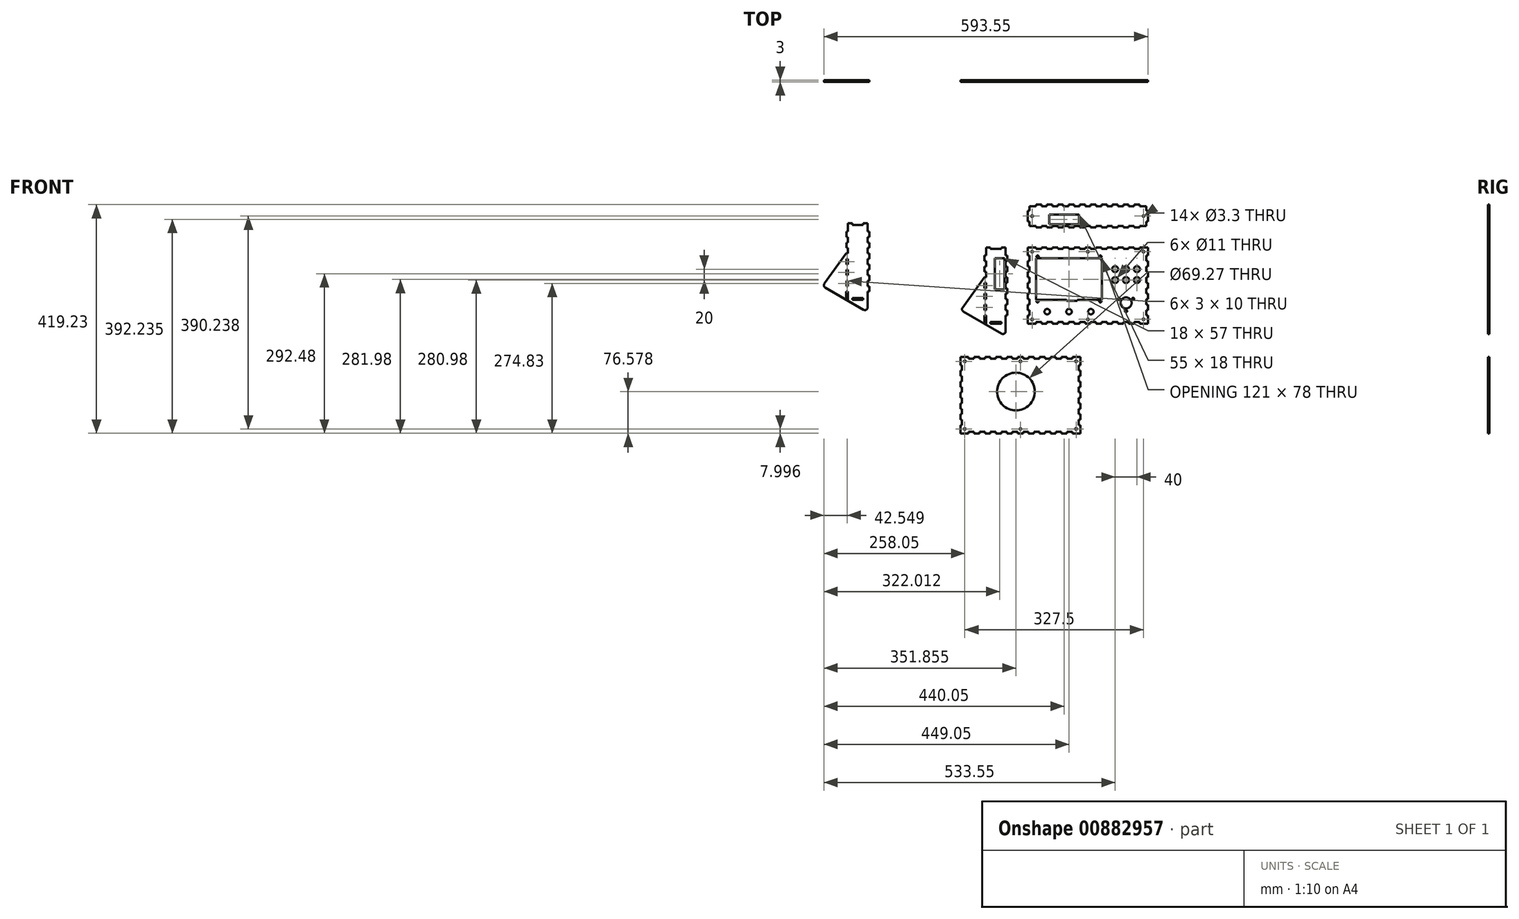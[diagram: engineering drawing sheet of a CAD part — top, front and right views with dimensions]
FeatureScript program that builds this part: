
annotation { "Feature Type Name" : "Feature", "Feature Type Description" : "" }
export const myFeature = defineFeature(function(context is Context, id is Id, definition is map)
    precondition{}
    {
        {
            var Q0;
            Q0=qCreatedBy(makeId("Front.planeOp"),FACE);
            var sketch = newSketch(context, id + "F0", { "sketchPlane" : qUnion([Q0])});
            skLineSegment(sketch, "E0.bottom", {"start": v(-60.5, 38) * mm, "end": v(60.5, 38) * mm});
            skLineSegment(sketch, "E0.top", {"start": v(-60.5, -38) * mm, "end": v(-4.5, -38) * mm});
            skLineSegment(sketch, "E0.left", {"start": v(-60.5, 38) * mm, "end": v(-60.5, -38) * mm});
            skLineSegment(sketch, "E0.right", {"start": v(60.5, 38) * mm, "end": v(60.5, -38) * mm});
            skPoint(sketch, "E0.middle", {"position": v(0, 0) * mm});
            skLineSegment(sketch, "E1.bottom", {"start": v(-75.5, -82) * mm, "end": v(-60.5, -82) * mm});
            skLineSegment(sketch, "E1.top", {"start": v(-75.5, 58) * mm, "end": v(-60.5, 58) * mm});
            skLineSegment(sketch, "E1.left", {"start": v(-75.5, -82) * mm, "end": v(-75.5, -67) * mm});
            skLineSegment(sketch, "E2", {"start": v(-75.5, 43) * mm, "end": v(-72.5, 43) * mm});
            skLineSegment(sketch, "E3", {"start": v(-72.5, 43) * mm, "end": v(-72.5, 33) * mm});
            skLineSegment(sketch, "E4", {"start": v(-72.5, 33) * mm, "end": v(-75.5, 33) * mm});
            skLineSegment(sketch, "E5.0.1.0", {"start": v(-75.5, 23) * mm, "end": v(-72.5, 23) * mm});
            skLineSegment(sketch, "E5.0.1.1", {"start": v(-72.5, 23) * mm, "end": v(-72.5, 13) * mm});
            skLineSegment(sketch, "E5.0.1.2", {"start": v(-72.5, 13) * mm, "end": v(-75.5, 13) * mm});
            skLineSegment(sketch, "E5.0.2.0", {"start": v(-75.5, 3) * mm, "end": v(-72.5, 3) * mm});
            skLineSegment(sketch, "E5.0.2.1", {"start": v(-72.5, 3) * mm, "end": v(-72.5, -7) * mm});
            skLineSegment(sketch, "E5.0.2.2", {"start": v(-72.5, -7) * mm, "end": v(-75.5, -7) * mm});
            skLineSegment(sketch, "E5.0.3.0", {"start": v(-75.5, -17) * mm, "end": v(-72.5, -17) * mm});
            skLineSegment(sketch, "E5.0.3.1", {"start": v(-72.5, -17) * mm, "end": v(-72.5, -27) * mm});
            skLineSegment(sketch, "E5.0.3.2", {"start": v(-72.5, -27) * mm, "end": v(-75.5, -27) * mm});
            skLineSegment(sketch, "E5.0.4.0", {"start": v(-75.5, -37) * mm, "end": v(-72.5, -37) * mm});
            skLineSegment(sketch, "E5.0.4.1", {"start": v(-72.5, -37) * mm, "end": v(-72.5, -47) * mm});
            skLineSegment(sketch, "E5.0.4.2", {"start": v(-72.5, -47) * mm, "end": v(-75.5, -47) * mm});
            skLineSegment(sketch, "E5.0.5.0", {"start": v(-75.5, -57) * mm, "end": v(-72.5, -57) * mm});
            skLineSegment(sketch, "E5.0.5.1", {"start": v(-72.5, -57) * mm, "end": v(-72.5, -67) * mm});
            skLineSegment(sketch, "E5.0.5.2", {"start": v(-72.5, -67) * mm, "end": v(-75.5, -67) * mm});
            skLineSegment(sketch, "E5.direction1", {"start": v(-75.5, 43) * mm, "end": v(-45.5, 43) * mm, "construction": true});
            skLineSegment(sketch, "E5.direction2", {"start": v(-75.5, 33) * mm, "end": v(-75.5, 23) * mm, "construction": true});
            skLineSegment(sketch, "E6.2.0.0", {"start": v(144.5, -79) * mm, "end": v(144.5, -82) * mm});
            skLineSegment(sketch, "E6.4.0.0", {"start": v(99.5, -79) * mm, "end": v(99.5, -82) * mm});
            skLineSegment(sketch, "E6.4.0.1", {"start": v(109.5, -79) * mm, "end": v(99.5, -79) * mm});
            skLineSegment(sketch, "E6.4.0.2", {"start": v(109.5, -82) * mm, "end": v(109.5, -79) * mm});
            skLineSegment(sketch, "E6.5.0.0", {"start": v(79.5, -79) * mm, "end": v(79.5, -82) * mm});
            skLineSegment(sketch, "E6.5.0.1", {"start": v(89.5, -79) * mm, "end": v(79.5, -79) * mm});
            skLineSegment(sketch, "E6.5.0.2", {"start": v(89.5, -82) * mm, "end": v(89.5, -79) * mm});
            skLineSegment(sketch, "E6.6.0.0", {"start": v(59.5, -79) * mm, "end": v(59.5, -82) * mm});
            skLineSegment(sketch, "E6.6.0.1", {"start": v(69.5, -79) * mm, "end": v(59.5, -79) * mm});
            skLineSegment(sketch, "E6.6.0.2", {"start": v(69.5, -82) * mm, "end": v(69.5, -79) * mm});
            skLineSegment(sketch, "E6.7.0.0", {"start": v(39.5, -79) * mm, "end": v(39.5, -82) * mm});
            skLineSegment(sketch, "E6.7.0.1", {"start": v(49.5, -79) * mm, "end": v(39.5, -79) * mm});
            skLineSegment(sketch, "E6.7.0.2", {"start": v(49.5, -82) * mm, "end": v(49.5, -79) * mm});
            skLineSegment(sketch, "E6.8.0.0", {"start": v(19.5, -79) * mm, "end": v(19.5, -82) * mm});
            skLineSegment(sketch, "E6.8.0.1", {"start": v(29.5, -79) * mm, "end": v(19.5, -79) * mm});
            skLineSegment(sketch, "E6.8.0.2", {"start": v(29.5, -82) * mm, "end": v(29.5, -79) * mm});
            skLineSegment(sketch, "E6.9.0.0", {"start": v(-0.5, -79) * mm, "end": v(-0.5, -82) * mm});
            skLineSegment(sketch, "E6.9.0.1", {"start": v(9.5, -79) * mm, "end": v(-0.5, -79) * mm});
            skLineSegment(sketch, "E6.9.0.2", {"start": v(9.5, -82) * mm, "end": v(9.5, -79) * mm});
            skLineSegment(sketch, "E6.10.0.0", {"start": v(-20.5, -79) * mm, "end": v(-20.5, -82) * mm});
            skLineSegment(sketch, "E6.10.0.1", {"start": v(-10.5, -79) * mm, "end": v(-20.5, -79) * mm});
            skLineSegment(sketch, "E6.10.0.2", {"start": v(-10.5, -82) * mm, "end": v(-10.5, -79) * mm});
            skLineSegment(sketch, "E6.11.0.0", {"start": v(-40.5, -79) * mm, "end": v(-40.5, -82) * mm});
            skLineSegment(sketch, "E6.11.0.1", {"start": v(-30.5, -79) * mm, "end": v(-40.5, -79) * mm});
            skLineSegment(sketch, "E6.11.0.2", {"start": v(-30.5, -82) * mm, "end": v(-30.5, -79) * mm});
            skLineSegment(sketch, "E6.12.0.0", {"start": v(-60.5, -79) * mm, "end": v(-60.5, -82) * mm});
            skLineSegment(sketch, "E6.12.0.1", {"start": v(-50.5, -79) * mm, "end": v(-60.5, -79) * mm});
            skLineSegment(sketch, "E6.12.0.2", {"start": v(-50.5, -82) * mm, "end": v(-50.5, -79) * mm});
            skLineSegment(sketch, "E7.2.0.2", {"start": v(144.5, 55) * mm, "end": v(144.5, 58) * mm});
            skLineSegment(sketch, "E7.3.0.0", {"start": v(129.5, 55) * mm, "end": v(119.5, 55) * mm});
            skLineSegment(sketch, "E7.3.0.1", {"start": v(129.5, 58) * mm, "end": v(129.5, 55) * mm});
            skLineSegment(sketch, "E7.3.0.2", {"start": v(119.5, 55) * mm, "end": v(119.5, 58) * mm});
            skLineSegment(sketch, "E7.4.0.0", {"start": v(109.5, 55) * mm, "end": v(99.5, 55) * mm});
            skLineSegment(sketch, "E7.4.0.1", {"start": v(109.5, 58) * mm, "end": v(109.5, 55) * mm});
            skLineSegment(sketch, "E7.4.0.2", {"start": v(99.5, 55) * mm, "end": v(99.5, 58) * mm});
            skLineSegment(sketch, "E7.5.0.0", {"start": v(89.5, 55) * mm, "end": v(79.5, 55) * mm});
            skLineSegment(sketch, "E7.5.0.1", {"start": v(89.5, 58) * mm, "end": v(89.5, 55) * mm});
            skLineSegment(sketch, "E7.5.0.2", {"start": v(79.5, 55) * mm, "end": v(79.5, 58) * mm});
            skLineSegment(sketch, "E7.6.0.0", {"start": v(69.5, 55) * mm, "end": v(59.5, 55) * mm});
            skLineSegment(sketch, "E7.6.0.1", {"start": v(69.5, 58) * mm, "end": v(69.5, 55) * mm});
            skLineSegment(sketch, "E7.6.0.2", {"start": v(59.5, 55) * mm, "end": v(59.5, 58) * mm});
            skLineSegment(sketch, "E7.7.0.0", {"start": v(49.5, 55) * mm, "end": v(39.5, 55) * mm});
            skLineSegment(sketch, "E7.7.0.1", {"start": v(49.5, 58) * mm, "end": v(49.5, 55) * mm});
            skLineSegment(sketch, "E7.7.0.2", {"start": v(39.5, 55) * mm, "end": v(39.5, 58) * mm});
            skLineSegment(sketch, "E7.8.0.0", {"start": v(29.5, 55) * mm, "end": v(19.5, 55) * mm});
            skLineSegment(sketch, "E7.8.0.1", {"start": v(29.5, 58) * mm, "end": v(29.5, 55) * mm});
            skLineSegment(sketch, "E7.8.0.2", {"start": v(19.5, 55) * mm, "end": v(19.5, 58) * mm});
            skLineSegment(sketch, "E7.9.0.0", {"start": v(9.5, 55) * mm, "end": v(-0.5, 55) * mm});
            skLineSegment(sketch, "E7.9.0.1", {"start": v(9.5, 58) * mm, "end": v(9.5, 55) * mm});
            skLineSegment(sketch, "E7.9.0.2", {"start": v(-0.5, 55) * mm, "end": v(-0.5, 58) * mm});
            skLineSegment(sketch, "E7.10.0.0", {"start": v(-10.5, 55) * mm, "end": v(-20.5, 55) * mm});
            skLineSegment(sketch, "E7.10.0.1", {"start": v(-10.5, 58) * mm, "end": v(-10.5, 55) * mm});
            skLineSegment(sketch, "E7.10.0.2", {"start": v(-20.5, 55) * mm, "end": v(-20.5, 58) * mm});
            skLineSegment(sketch, "E7.11.0.0", {"start": v(-30.5, 55) * mm, "end": v(-40.5, 55) * mm});
            skLineSegment(sketch, "E7.11.0.1", {"start": v(-30.5, 58) * mm, "end": v(-30.5, 55) * mm});
            skLineSegment(sketch, "E7.11.0.2", {"start": v(-40.5, 55) * mm, "end": v(-40.5, 58) * mm});
            skLineSegment(sketch, "E7.12.0.0", {"start": v(-50.5, 55) * mm, "end": v(-60.5, 55) * mm});
            skLineSegment(sketch, "E7.12.0.1", {"start": v(-50.5, 58) * mm, "end": v(-50.5, 55) * mm});
            skLineSegment(sketch, "E7.12.0.2", {"start": v(-60.5, 55) * mm, "end": v(-60.5, 58) * mm});
            skLineSegment(sketch, "E8.trimOffspring", {"start": v(-50.5, 58) * mm, "end": v(-40.5, 58) * mm});
            skLineSegment(sketch, "E9.trimOffspring", {"start": v(-30.5, 58) * mm, "end": v(-20.5, 58) * mm});
            skLineSegment(sketch, "E10.trimOffspring", {"start": v(-10.5, 58) * mm, "end": v(-0.5, 58) * mm});
            skLineSegment(sketch, "E11.trimOffspring", {"start": v(9.5, 58) * mm, "end": v(19.5, 58) * mm});
            skLineSegment(sketch, "E12.trimOffspring", {"start": v(29.5, 58) * mm, "end": v(39.5, 58) * mm});
            skLineSegment(sketch, "E13.trimOffspring", {"start": v(49.5, 58) * mm, "end": v(59.5, 58) * mm});
            skLineSegment(sketch, "E14.trimOffspring", {"start": v(69.5, 58) * mm, "end": v(79.5, 58) * mm});
            skLineSegment(sketch, "E15.trimOffspring", {"start": v(89.5, 58) * mm, "end": v(99.5, 58) * mm});
            skLineSegment(sketch, "E16.trimOffspring", {"start": v(109.5, 58) * mm, "end": v(119.5, 58) * mm});
            skLineSegment(sketch, "E17.trimOffspring", {"start": v(-75.5, 23) * mm, "end": v(-75.5, 33) * mm});
            skLineSegment(sketch, "E18.trimOffspring", {"start": v(129.5, 58) * mm, "end": v(144.5, 58) * mm});
            skLineSegment(sketch, "E19.trimOffspring", {"start": v(129.5, -82) * mm, "end": v(144.5, -82) * mm});
            skLineSegment(sketch, "E20.trimOffspring", {"start": v(89.5, -82) * mm, "end": v(99.5, -82) * mm});
            skLineSegment(sketch, "E21.trimOffspring", {"start": v(69.5, -82) * mm, "end": v(79.5, -82) * mm});
            skLineSegment(sketch, "E22.trimOffspring", {"start": v(49.5, -82) * mm, "end": v(59.5, -82) * mm});
            skLineSegment(sketch, "E23.trimOffspring", {"start": v(29.5, -82) * mm, "end": v(39.5, -82) * mm});
            skLineSegment(sketch, "E24.trimOffspring", {"start": v(9.5, -82) * mm, "end": v(19.5, -82) * mm});
            skLineSegment(sketch, "E25.trimOffspring", {"start": v(-10.5, -82) * mm, "end": v(-0.5, -82) * mm});
            skLineSegment(sketch, "E26.trimOffspring", {"start": v(-30.5, -82) * mm, "end": v(-20.5, -82) * mm});
            skLineSegment(sketch, "E27.trimOffspring", {"start": v(-50.5, -82) * mm, "end": v(-40.5, -82) * mm});
            skLineSegment(sketch, "E28.trimOffspring", {"start": v(-75.5, -57) * mm, "end": v(-75.5, -47) * mm});
            skLineSegment(sketch, "E29.trimOffspring", {"start": v(-75.5, -37) * mm, "end": v(-75.5, -27) * mm});
            skLineSegment(sketch, "E30.trimOffspring", {"start": v(-75.5, -17) * mm, "end": v(-75.5, -7) * mm});
            skLineSegment(sketch, "E31.trimOffspring", {"start": v(-75.5, 3) * mm, "end": v(-75.5, 13) * mm});
            skLineSegment(sketch, "E32.trimOffspring", {"start": v(-75.5, 43) * mm, "end": v(-75.5, 58) * mm});
            skLineSegment(sketch, "E33.bottom", {"start": v(-116.04, 58) * mm, "end": v(-124.04, 58) * mm});
            skLineSegment(sketch, "E33.left", {"start": v(-116.04, 58) * mm, "end": v(-116.04, 43) * mm});
            skLineSegment(sketch, "E33.right", {"start": v(-152.04, 58) * mm, "end": v(-152.04, 43) * mm});
            skLineSegment(sketch, "E34", {"start": v(-116.04, 43) * mm, "end": v(-113.04, 43) * mm});
            skLineSegment(sketch, "E35", {"start": v(-113.04, 43) * mm, "end": v(-113.04, 33) * mm});
            skLineSegment(sketch, "E36", {"start": v(-113.04, 33) * mm, "end": v(-116.04, 33) * mm});
            skLineSegment(sketch, "E37.0.1.0", {"start": v(-116.04, 23) * mm, "end": v(-113.04, 23) * mm});
            skLineSegment(sketch, "E37.0.1.1", {"start": v(-113.04, 23) * mm, "end": v(-113.04, 13) * mm});
            skLineSegment(sketch, "E37.0.1.2", {"start": v(-113.04, 13) * mm, "end": v(-116.04, 13) * mm});
            skLineSegment(sketch, "E37.0.2.0", {"start": v(-116.04, 3) * mm, "end": v(-113.04, 3) * mm});
            skLineSegment(sketch, "E37.0.2.1", {"start": v(-113.04, 3) * mm, "end": v(-113.04, -7) * mm});
            skLineSegment(sketch, "E37.0.2.2", {"start": v(-113.04, -7) * mm, "end": v(-116.04, -7) * mm});
            skLineSegment(sketch, "E37.0.3.0", {"start": v(-116.04, -17) * mm, "end": v(-113.04, -17) * mm});
            skLineSegment(sketch, "E37.0.3.1", {"start": v(-113.04, -17) * mm, "end": v(-113.04, -27) * mm});
            skLineSegment(sketch, "E37.0.3.2", {"start": v(-113.04, -27) * mm, "end": v(-116.04, -27) * mm});
            skLineSegment(sketch, "E37.0.4.0", {"start": v(-116.04, -37) * mm, "end": v(-113.04, -37) * mm});
            skLineSegment(sketch, "E37.0.4.1", {"start": v(-113.04, -37) * mm, "end": v(-113.04, -47) * mm});
            skLineSegment(sketch, "E37.0.4.2", {"start": v(-113.04, -47) * mm, "end": v(-116.04, -47) * mm});
            skLineSegment(sketch, "E37.0.5.0", {"start": v(-116.04, -57) * mm, "end": v(-113.04, -57) * mm});
            skLineSegment(sketch, "E37.0.5.1", {"start": v(-113.04, -57) * mm, "end": v(-113.04, -67) * mm});
            skLineSegment(sketch, "E37.0.5.2", {"start": v(-113.04, -67) * mm, "end": v(-116.04, -67) * mm});
            skLineSegment(sketch, "E37.direction1", {"start": v(-116.04, 43) * mm, "end": v(-91.54, 43) * mm, "construction": true});
            skLineSegment(sketch, "E37.direction2", {"start": v(-116.04, 33) * mm, "end": v(-116.04, 23) * mm, "construction": true});
            skLineSegment(sketch, "E38.trimOffspring", {"start": v(-116.04, 13) * mm, "end": v(-116.04, 3) * mm});
            skLineSegment(sketch, "E39.trimOffspring", {"start": v(-116.04, 33) * mm, "end": v(-116.04, 23) * mm});
            skLineSegment(sketch, "E40.trimOffspring", {"start": v(-116.04, -7) * mm, "end": v(-116.04, -17) * mm});
            skLineSegment(sketch, "E41.trimOffspring", {"start": v(-116.04, -27) * mm, "end": v(-116.04, -37) * mm});
            skLineSegment(sketch, "E42.trimOffspring", {"start": v(-116.04, -47) * mm, "end": v(-116.04, -57) * mm});
            skLineSegment(sketch, "E43.trimOffspring", {"start": v(-116.04, -67) * mm, "end": v(-116.04, -82) * mm});
            skLineSegment(sketch, "E44", {"start": v(-152.04, 43) * mm, "end": v(-155.04, 43) * mm});
            skLineSegment(sketch, "E45", {"start": v(-155.04, 43) * mm, "end": v(-155.04, 33) * mm});
            skLineSegment(sketch, "E46", {"start": v(-155.04, 33) * mm, "end": v(-152.04, 33) * mm});
            skLineSegment(sketch, "E47.0.1.0", {"start": v(-152.04, 23) * mm, "end": v(-155.04, 23) * mm});
            skLineSegment(sketch, "E47.0.1.1", {"start": v(-155.04, 23) * mm, "end": v(-155.04, 13) * mm});
            skLineSegment(sketch, "E47.0.1.2", {"start": v(-155.04, 13) * mm, "end": v(-152.04, 13) * mm});
            skLineSegment(sketch, "E47.0.2.0", {"start": v(-152.04, 3) * mm, "end": v(-155.04, 3) * mm});
            skLineSegment(sketch, "E47.0.2.2", {"start": v(-155.04, -7) * mm, "end": v(-152.04, -7) * mm});
            skLineSegment(sketch, "E47.0.3.0", {"start": v(-152.04, -17) * mm, "end": v(-155.04, -17) * mm});
            skLineSegment(sketch, "E47.0.3.2", {"start": v(-155.04, -27) * mm, "end": v(-152.04, -27) * mm});
            skLineSegment(sketch, "E47.0.4.0", {"start": v(-152.04, -37) * mm, "end": v(-155.04, -37) * mm});
            skLineSegment(sketch, "E47.0.4.2", {"start": v(-155.04, -47) * mm, "end": v(-152.04, -47) * mm});
            skLineSegment(sketch, "E47.0.5.0", {"start": v(-152.04, -57) * mm, "end": v(-155.04, -57) * mm});
            skLineSegment(sketch, "E47.0.5.2", {"start": v(-155.04, -67) * mm, "end": v(-152.04, -67) * mm});
            skLineSegment(sketch, "E47.direction1", {"start": v(-155.04, 43) * mm, "end": v(-130.54, 43) * mm, "construction": true});
            skLineSegment(sketch, "E47.direction2", {"start": v(-155.04, 43) * mm, "end": v(-155.04, 23) * mm, "construction": true});
            skLineSegment(sketch, "E48.trimOffspring", {"start": v(-152.04, 33) * mm, "end": v(-152.04, 23) * mm});
            skLineSegment(sketch, "E49.trimOffspring", {"start": v(-152.04, 13) * mm, "end": v(-152.04, 3) * mm});
            skLineSegment(sketch, "E50.trimOffspring", {"start": v(-152.04, -7) * mm, "end": v(-152.04, -17) * mm});
            skLineSegment(sketch, "E51", {"start": v(-155.04, -67) * mm, "end": v(-155.04, -82) * mm});
            skLineSegment(sketch, "E52.trimOffspring", {"start": v(-152.04, -67) * mm, "end": v(-152.04, -82) * mm});
            skLineSegment(sketch, "E53", {"start": v(-155.04, -47) * mm, "end": v(-155.04, -57) * mm});
            skLineSegment(sketch, "E54", {"start": v(-155.04, -27) * mm, "end": v(-155.04, -37) * mm});
            skLineSegment(sketch, "E55.trimOffspring", {"start": v(-152.04, -47) * mm, "end": v(-152.04, -57) * mm});
            skLineSegment(sketch, "E56.trimOffspring", {"start": v(-152.04, -27) * mm, "end": v(-152.04, -37) * mm});
            skLineSegment(sketch, "E57", {"start": v(-155.04, -82) * mm, "end": v(-193.55, -59.77) * mm});
            skLineSegment(sketch, "E58", {"start": v(-155.04, -17) * mm, "end": v(-155.04, -7) * mm});
            skLineSegment(sketch, "E59", {"start": v(-195.1, -52.51) * mm, "end": v(-155.04, 3) * mm});
            skPoint(sketch, "E60.visualSharp", {"position": v(-198.34, -57) * mm});
            skArc(sketch, "E60.filletArc", {"start": v(-195.1, -52.51) * mm, "mid": v(-195.93, -56.48) * mm, "end": v(-193.55, -59.77) * mm});
            skLineSegment(sketch, "E61.bottom", {"start": v(-136.04, 38) * mm, "end": v(-118.04, 38) * mm});
            skLineSegment(sketch, "E61.top", {"start": v(-136.04, -19) * mm, "end": v(-118.04, -19) * mm});
            skLineSegment(sketch, "E61.left", {"start": v(-136.04, 38) * mm, "end": v(-136.04, -19) * mm});
            skLineSegment(sketch, "E61.right", {"start": v(-118.04, 38) * mm, "end": v(-118.04, -19) * mm});
            skLineSegment(sketch, "E62.bottom", {"start": v(-369, 101.85) * mm, "end": v(-377, 101.85) * mm});
            skLineSegment(sketch, "E62.left", {"start": v(-369, 101.85) * mm, "end": v(-369, 86.85) * mm});
            skLineSegment(sketch, "E62.right", {"start": v(-405, 101.85) * mm, "end": v(-405, 86.85) * mm});
            skLineSegment(sketch, "E63", {"start": v(-369, 86.85) * mm, "end": v(-366, 86.85) * mm});
            skLineSegment(sketch, "E64", {"start": v(-366, 86.85) * mm, "end": v(-366, 76.85) * mm});
            skLineSegment(sketch, "E65", {"start": v(-366, 76.85) * mm, "end": v(-369, 76.85) * mm});
            skLineSegment(sketch, "E66.0.1.0", {"start": v(-369, 66.85) * mm, "end": v(-366, 66.85) * mm});
            skLineSegment(sketch, "E66.0.1.1", {"start": v(-366, 66.85) * mm, "end": v(-366, 56.85) * mm});
            skLineSegment(sketch, "E66.0.1.2", {"start": v(-366, 56.85) * mm, "end": v(-369, 56.85) * mm});
            skLineSegment(sketch, "E66.0.2.0", {"start": v(-369, 46.85) * mm, "end": v(-366, 46.85) * mm});
            skLineSegment(sketch, "E66.0.2.1", {"start": v(-366, 46.85) * mm, "end": v(-366, 36.85) * mm});
            skLineSegment(sketch, "E66.0.2.2", {"start": v(-366, 36.85) * mm, "end": v(-369, 36.85) * mm});
            skLineSegment(sketch, "E66.0.3.0", {"start": v(-369, 26.85) * mm, "end": v(-366, 26.85) * mm});
            skLineSegment(sketch, "E66.0.3.1", {"start": v(-366, 26.85) * mm, "end": v(-366, 16.85) * mm});
            skLineSegment(sketch, "E66.0.3.2", {"start": v(-366, 16.85) * mm, "end": v(-369, 16.85) * mm});
            skLineSegment(sketch, "E66.0.4.0", {"start": v(-369, 6.85) * mm, "end": v(-366, 6.85) * mm});
            skLineSegment(sketch, "E66.0.4.1", {"start": v(-366, 6.85) * mm, "end": v(-366, -3.15) * mm});
            skLineSegment(sketch, "E66.0.4.2", {"start": v(-366, -3.15) * mm, "end": v(-369, -3.15) * mm});
            skLineSegment(sketch, "E66.0.5.0", {"start": v(-369, -13.15) * mm, "end": v(-366, -13.15) * mm});
            skLineSegment(sketch, "E66.0.5.1", {"start": v(-366, -13.15) * mm, "end": v(-366, -23.15) * mm});
            skLineSegment(sketch, "E66.0.5.2", {"start": v(-366, -23.15) * mm, "end": v(-369, -23.15) * mm});
            skLineSegment(sketch, "E66.direction2", {"start": v(-369, 76.85) * mm, "end": v(-369, 66.85) * mm, "construction": true});
            skLineSegment(sketch, "E67.trimOffspring", {"start": v(-369, 56.85) * mm, "end": v(-369, 46.85) * mm});
            skLineSegment(sketch, "E68.trimOffspring", {"start": v(-369, 76.85) * mm, "end": v(-369, 66.85) * mm});
            skLineSegment(sketch, "E69.trimOffspring", {"start": v(-369, 36.85) * mm, "end": v(-369, 26.85) * mm});
            skLineSegment(sketch, "E70.trimOffspring", {"start": v(-369, 16.85) * mm, "end": v(-369, 6.85) * mm});
            skLineSegment(sketch, "E71.trimOffspring", {"start": v(-369, -3.15) * mm, "end": v(-369, -13.15) * mm});
            skLineSegment(sketch, "E72.trimOffspring", {"start": v(-369, -23.15) * mm, "end": v(-369, -38.15) * mm});
            skLineSegment(sketch, "E73", {"start": v(-405, 86.85) * mm, "end": v(-408, 86.85) * mm});
            skLineSegment(sketch, "E74", {"start": v(-408, 86.85) * mm, "end": v(-408, 76.85) * mm});
            skLineSegment(sketch, "E75", {"start": v(-408, 76.85) * mm, "end": v(-405, 76.85) * mm});
            skLineSegment(sketch, "E76.0.1.0", {"start": v(-405, 66.85) * mm, "end": v(-408, 66.85) * mm});
            skLineSegment(sketch, "E76.0.1.1", {"start": v(-408, 66.85) * mm, "end": v(-408, 56.85) * mm});
            skLineSegment(sketch, "E76.0.1.2", {"start": v(-408, 56.85) * mm, "end": v(-405, 56.85) * mm});
            skLineSegment(sketch, "E76.0.2.0", {"start": v(-405, 46.85) * mm, "end": v(-408.04, 46.85) * mm});
            skLineSegment(sketch, "E76.0.2.2", {"start": v(-408, 36.85) * mm, "end": v(-405, 36.85) * mm});
            skLineSegment(sketch, "E76.0.3.0", {"start": v(-405, 26.85) * mm, "end": v(-408, 26.85) * mm});
            skLineSegment(sketch, "E76.0.3.2", {"start": v(-408, 16.85) * mm, "end": v(-405, 16.85) * mm});
            skLineSegment(sketch, "E76.0.4.0", {"start": v(-405, 6.85) * mm, "end": v(-408, 6.85) * mm});
            skLineSegment(sketch, "E76.0.4.2", {"start": v(-408, -3.15) * mm, "end": v(-405, -3.15) * mm});
            skLineSegment(sketch, "E76.0.5.0", {"start": v(-405, -13.15) * mm, "end": v(-408, -13.15) * mm});
            skLineSegment(sketch, "E76.0.5.2", {"start": v(-408.04, -23.15) * mm, "end": v(-405, -23.15) * mm});
            skLineSegment(sketch, "E76.direction1", {"start": v(-408, 86.85) * mm, "end": v(-383.04, 86.85) * mm, "construction": true});
            skLineSegment(sketch, "E76.direction2", {"start": v(-408, 86.85) * mm, "end": v(-408, 66.85) * mm, "construction": true});
            skLineSegment(sketch, "E77.trimOffspring", {"start": v(-405, 76.85) * mm, "end": v(-405, 66.85) * mm});
            skLineSegment(sketch, "E78.trimOffspring", {"start": v(-405, 56.85) * mm, "end": v(-405, 46.85) * mm});
            skLineSegment(sketch, "E79.trimOffspring", {"start": v(-405, 36.85) * mm, "end": v(-405, 26.85) * mm});
            skLineSegment(sketch, "E80", {"start": v(-408.04, -23.15) * mm, "end": v(-408.04, -38.14) * mm});
            skLineSegment(sketch, "E81.trimOffspring", {"start": v(-405, -23.15) * mm, "end": v(-405, -38.15) * mm});
            skLineSegment(sketch, "E82", {"start": v(-408, -3.15) * mm, "end": v(-408, -13.15) * mm});
            skLineSegment(sketch, "E83", {"start": v(-408, 16.85) * mm, "end": v(-408, 6.85) * mm});
            skLineSegment(sketch, "E84.trimOffspring", {"start": v(-405, -3.15) * mm, "end": v(-405, -13.15) * mm});
            skLineSegment(sketch, "E85.trimOffspring", {"start": v(-405, 16.85) * mm, "end": v(-405, 6.85) * mm});
            skLineSegment(sketch, "E86", {"start": v(-408.04, -38.15) * mm, "end": v(-446.55, -15.92) * mm});
            skLineSegment(sketch, "E87", {"start": v(-408, 26.85) * mm, "end": v(-408, 36.85) * mm});
            skLineSegment(sketch, "E88", {"start": v(-448.1, -8.66) * mm, "end": v(-408.04, 46.85) * mm});
            skPoint(sketch, "E89.visualSharp", {"position": v(-451.35, -13.15) * mm});
            skArc(sketch, "E89.filletArc", {"start": v(-448.1, -8.66) * mm, "mid": v(-448.94, -12.63) * mm, "end": v(-446.55, -15.92) * mm});
            skLineSegment(sketch, "E90.top", {"start": v(-199, -142.98) * mm, "end": v(-184, -142.98) * mm});
            skLineSegment(sketch, "E90.left", {"start": v(-199, -282.98) * mm, "end": v(-199, -267.98) * mm});
            skLineSegment(sketch, "E91", {"start": v(-199, -157.98) * mm, "end": v(-196, -157.98) * mm});
            skLineSegment(sketch, "E92", {"start": v(-196, -157.98) * mm, "end": v(-196, -167.98) * mm});
            skLineSegment(sketch, "E93", {"start": v(-196, -167.98) * mm, "end": v(-199, -167.98) * mm});
            skLineSegment(sketch, "E94.0.1.0", {"start": v(-199, -177.98) * mm, "end": v(-196, -177.98) * mm});
            skLineSegment(sketch, "E94.0.1.1", {"start": v(-196, -177.98) * mm, "end": v(-196, -187.98) * mm});
            skLineSegment(sketch, "E94.0.1.2", {"start": v(-196, -187.98) * mm, "end": v(-199, -187.98) * mm});
            skLineSegment(sketch, "E94.0.2.0", {"start": v(-199, -197.98) * mm, "end": v(-196, -197.98) * mm});
            skLineSegment(sketch, "E94.0.2.1", {"start": v(-196, -197.98) * mm, "end": v(-196, -207.98) * mm});
            skLineSegment(sketch, "E94.0.2.2", {"start": v(-196, -207.98) * mm, "end": v(-199, -207.98) * mm});
            skLineSegment(sketch, "E94.0.3.0", {"start": v(-199, -217.98) * mm, "end": v(-196, -217.98) * mm});
            skLineSegment(sketch, "E94.0.3.1", {"start": v(-196, -217.98) * mm, "end": v(-196, -227.98) * mm});
            skLineSegment(sketch, "E94.0.3.2", {"start": v(-196, -227.98) * mm, "end": v(-199, -227.98) * mm});
            skLineSegment(sketch, "E94.0.4.0", {"start": v(-199, -237.98) * mm, "end": v(-196, -237.98) * mm});
            skLineSegment(sketch, "E94.0.4.1", {"start": v(-196, -237.98) * mm, "end": v(-196, -247.98) * mm});
            skLineSegment(sketch, "E94.0.4.2", {"start": v(-196, -247.98) * mm, "end": v(-199, -247.98) * mm});
            skLineSegment(sketch, "E94.0.5.0", {"start": v(-199, -257.98) * mm, "end": v(-196, -257.98) * mm});
            skLineSegment(sketch, "E94.0.5.1", {"start": v(-196, -257.98) * mm, "end": v(-196, -267.98) * mm});
            skLineSegment(sketch, "E94.0.5.2", {"start": v(-196, -267.98) * mm, "end": v(-199, -267.98) * mm});
            skLineSegment(sketch, "E94.direction2", {"start": v(-199, -167.98) * mm, "end": v(-199, -177.98) * mm, "construction": true});
            skLineSegment(sketch, "E95.2.0.2", {"start": v(21, -145.98) * mm, "end": v(21, -142.98) * mm});
            skLineSegment(sketch, "E95.3.0.0", {"start": v(6, -145.98) * mm, "end": v(-4, -145.98) * mm});
            skLineSegment(sketch, "E95.3.0.1", {"start": v(6, -142.98) * mm, "end": v(6, -145.98) * mm});
            skLineSegment(sketch, "E95.3.0.2", {"start": v(-4, -145.98) * mm, "end": v(-4, -142.98) * mm});
            skLineSegment(sketch, "E95.4.0.0", {"start": v(-14, -145.98) * mm, "end": v(-24, -145.98) * mm});
            skLineSegment(sketch, "E95.4.0.1", {"start": v(-14, -142.98) * mm, "end": v(-14, -145.98) * mm});
            skLineSegment(sketch, "E95.4.0.2", {"start": v(-24, -145.98) * mm, "end": v(-24, -142.98) * mm});
            skLineSegment(sketch, "E95.5.0.0", {"start": v(-34, -145.98) * mm, "end": v(-44, -145.98) * mm});
            skLineSegment(sketch, "E95.5.0.1", {"start": v(-34, -142.98) * mm, "end": v(-34, -145.98) * mm});
            skLineSegment(sketch, "E95.5.0.2", {"start": v(-44, -145.98) * mm, "end": v(-44, -142.98) * mm});
            skLineSegment(sketch, "E95.6.0.0", {"start": v(-54, -145.98) * mm, "end": v(-64, -145.98) * mm});
            skLineSegment(sketch, "E95.6.0.1", {"start": v(-54, -142.98) * mm, "end": v(-54, -145.98) * mm});
            skLineSegment(sketch, "E95.6.0.2", {"start": v(-64, -145.98) * mm, "end": v(-64, -142.98) * mm});
            skLineSegment(sketch, "E95.7.0.0", {"start": v(-74, -145.98) * mm, "end": v(-84, -145.98) * mm});
            skLineSegment(sketch, "E95.7.0.1", {"start": v(-74, -142.98) * mm, "end": v(-74, -145.98) * mm});
            skLineSegment(sketch, "E95.7.0.2", {"start": v(-84, -145.98) * mm, "end": v(-84, -142.98) * mm});
            skLineSegment(sketch, "E95.8.0.0", {"start": v(-94, -145.98) * mm, "end": v(-104, -145.98) * mm});
            skLineSegment(sketch, "E95.8.0.1", {"start": v(-94, -142.98) * mm, "end": v(-94, -145.98) * mm});
            skLineSegment(sketch, "E95.8.0.2", {"start": v(-104, -145.98) * mm, "end": v(-104, -142.98) * mm});
            skLineSegment(sketch, "E95.9.0.0", {"start": v(-114, -145.98) * mm, "end": v(-124, -145.98) * mm});
            skLineSegment(sketch, "E95.9.0.1", {"start": v(-114, -142.98) * mm, "end": v(-114, -145.98) * mm});
            skLineSegment(sketch, "E95.9.0.2", {"start": v(-124, -145.98) * mm, "end": v(-124, -142.98) * mm});
            skLineSegment(sketch, "E95.10.0.0", {"start": v(-134, -145.98) * mm, "end": v(-144, -145.98) * mm});
            skLineSegment(sketch, "E95.10.0.1", {"start": v(-134, -142.98) * mm, "end": v(-134, -145.98) * mm});
            skLineSegment(sketch, "E95.10.0.2", {"start": v(-144, -145.98) * mm, "end": v(-144, -142.98) * mm});
            skLineSegment(sketch, "E95.11.0.0", {"start": v(-154, -145.98) * mm, "end": v(-164, -145.98) * mm});
            skLineSegment(sketch, "E95.11.0.1", {"start": v(-154, -142.98) * mm, "end": v(-154, -145.98) * mm});
            skLineSegment(sketch, "E95.11.0.2", {"start": v(-164, -145.98) * mm, "end": v(-164, -142.98) * mm});
            skLineSegment(sketch, "E95.12.0.0", {"start": v(-174, -145.98) * mm, "end": v(-184, -145.98) * mm});
            skLineSegment(sketch, "E95.12.0.1", {"start": v(-174, -142.98) * mm, "end": v(-174, -145.98) * mm});
            skLineSegment(sketch, "E95.12.0.2", {"start": v(-184, -145.98) * mm, "end": v(-184, -142.98) * mm});
            skLineSegment(sketch, "E96.trimOffspring", {"start": v(-174, -142.98) * mm, "end": v(-164, -142.98) * mm});
            skLineSegment(sketch, "E97.trimOffspring", {"start": v(-154, -142.98) * mm, "end": v(-144, -142.98) * mm});
            skLineSegment(sketch, "E98.trimOffspring", {"start": v(-134, -142.98) * mm, "end": v(-124, -142.98) * mm});
            skLineSegment(sketch, "E99.trimOffspring", {"start": v(-114, -142.98) * mm, "end": v(-104, -142.98) * mm});
            skLineSegment(sketch, "E100.trimOffspring", {"start": v(-94, -142.98) * mm, "end": v(-84, -142.98) * mm});
            skLineSegment(sketch, "E101.trimOffspring", {"start": v(-74, -142.98) * mm, "end": v(-64, -142.98) * mm});
            skLineSegment(sketch, "E102.trimOffspring", {"start": v(-54, -142.98) * mm, "end": v(-44, -142.98) * mm});
            skLineSegment(sketch, "E103.trimOffspring", {"start": v(-34, -142.98) * mm, "end": v(-24, -142.98) * mm});
            skLineSegment(sketch, "E104.trimOffspring", {"start": v(-14, -142.98) * mm, "end": v(-4, -142.98) * mm});
            skLineSegment(sketch, "E105.trimOffspring", {"start": v(-199, -177.98) * mm, "end": v(-199, -167.98) * mm});
            skLineSegment(sketch, "E106.trimOffspring", {"start": v(6, -142.98) * mm, "end": v(21, -142.98) * mm});
            skLineSegment(sketch, "E107.trimOffspring", {"start": v(-199, -257.98) * mm, "end": v(-199, -247.98) * mm});
            skLineSegment(sketch, "E108.trimOffspring", {"start": v(-199, -237.98) * mm, "end": v(-199, -227.98) * mm});
            skLineSegment(sketch, "E109.trimOffspring", {"start": v(-199, -217.98) * mm, "end": v(-199, -207.98) * mm});
            skLineSegment(sketch, "E110.trimOffspring", {"start": v(-199, -197.98) * mm, "end": v(-199, -187.98) * mm});
            skLineSegment(sketch, "E111.trimOffspring", {"start": v(-199, -157.98) * mm, "end": v(-199, -142.98) * mm});
            skLineSegment(sketch, "E112.bottom", {"start": v(-60.5, 94.25) * mm, "end": v(-50.5, 94.25) * mm});
            skLineSegment(sketch, "E112.top", {"start": v(-60.5, 136.25) * mm, "end": v(-50.5, 136.25) * mm});
            skLineSegment(sketch, "E112.left", {"start": v(-75.5, 105.25) * mm, "end": v(-75.5, 125.25) * mm});
            skLineSegment(sketch, "E113", {"start": v(-60.5, 94.25) * mm, "end": v(-60.5, 97.25) * mm});
            skLineSegment(sketch, "E114", {"start": v(-60.5, 97.25) * mm, "end": v(-72.5, 97.25) * mm});
            skPoint(sketch, "E115.orphan", {"position": v(-75.5, 94.25) * mm});
            skLineSegment(sketch, "E116", {"start": v(-50.5, 94.25) * mm, "end": v(-50.5, 97.25) * mm});
            skLineSegment(sketch, "E117", {"start": v(-50.5, 97.25) * mm, "end": v(-40.5, 97.25) * mm});
            skLineSegment(sketch, "E118", {"start": v(-40.5, 97.25) * mm, "end": v(-40.5, 94.25) * mm});
            skLineSegment(sketch, "E119.trimOffspring", {"start": v(-40.5, 94.25) * mm, "end": v(-30.5, 94.25) * mm});
            skLineSegment(sketch, "E120.1.0.0", {"start": v(-30.5, 94.25) * mm, "end": v(-30.5, 97.25) * mm});
            skLineSegment(sketch, "E120.1.0.1", {"start": v(-30.5, 97.25) * mm, "end": v(-20.5, 97.25) * mm});
            skLineSegment(sketch, "E120.1.0.2", {"start": v(-20.5, 97.25) * mm, "end": v(-20.5, 94.25) * mm});
            skLineSegment(sketch, "E120.2.0.0", {"start": v(-10.5, 94.25) * mm, "end": v(-10.5, 97.25) * mm});
            skLineSegment(sketch, "E120.2.0.1", {"start": v(-10.5, 97.25) * mm, "end": v(-0.5, 97.25) * mm});
            skLineSegment(sketch, "E120.2.0.2", {"start": v(-0.5, 97.25) * mm, "end": v(-0.5, 94.25) * mm});
            skLineSegment(sketch, "E120.3.0.0", {"start": v(9.5, 94.25) * mm, "end": v(9.5, 97.25) * mm});
            skLineSegment(sketch, "E120.3.0.1", {"start": v(9.5, 97.25) * mm, "end": v(19.5, 97.25) * mm});
            skLineSegment(sketch, "E120.3.0.2", {"start": v(19.5, 97.25) * mm, "end": v(19.5, 94.25) * mm});
            skLineSegment(sketch, "E120.4.0.0", {"start": v(29.5, 94.25) * mm, "end": v(29.5, 97.25) * mm});
            skLineSegment(sketch, "E120.4.0.1", {"start": v(29.5, 97.25) * mm, "end": v(39.5, 97.25) * mm});
            skLineSegment(sketch, "E120.4.0.2", {"start": v(39.5, 97.25) * mm, "end": v(39.5, 94.25) * mm});
            skLineSegment(sketch, "E120.5.0.0", {"start": v(49.5, 94.25) * mm, "end": v(49.5, 97.25) * mm});
            skLineSegment(sketch, "E120.5.0.1", {"start": v(49.5, 97.25) * mm, "end": v(59.5, 97.25) * mm});
            skLineSegment(sketch, "E120.5.0.2", {"start": v(59.5, 97.25) * mm, "end": v(59.5, 94.25) * mm});
            skLineSegment(sketch, "E120.6.0.0", {"start": v(69.5, 94.25) * mm, "end": v(69.5, 97.25) * mm});
            skLineSegment(sketch, "E120.6.0.1", {"start": v(69.5, 97.25) * mm, "end": v(79.5, 97.25) * mm});
            skLineSegment(sketch, "E120.6.0.2", {"start": v(79.5, 97.25) * mm, "end": v(79.5, 94.25) * mm});
            skLineSegment(sketch, "E120.7.0.0", {"start": v(89.5, 94.25) * mm, "end": v(89.5, 97.25) * mm});
            skLineSegment(sketch, "E120.7.0.1", {"start": v(89.5, 97.25) * mm, "end": v(99.5, 97.25) * mm});
            skLineSegment(sketch, "E120.7.0.2", {"start": v(99.5, 97.25) * mm, "end": v(99.5, 94.25) * mm});
            skLineSegment(sketch, "E120.8.0.0", {"start": v(109.5, 94.25) * mm, "end": v(109.5, 97.25) * mm});
            skLineSegment(sketch, "E120.8.0.1", {"start": v(109.5, 97.25) * mm, "end": v(119.5, 97.25) * mm});
            skLineSegment(sketch, "E120.8.0.2", {"start": v(119.5, 97.25) * mm, "end": v(119.5, 94.25) * mm});
            skLineSegment(sketch, "E120.9.0.0", {"start": v(129.5, 94.25) * mm, "end": v(129.5, 97.25) * mm});
            skLineSegment(sketch, "E120.9.0.1", {"start": v(129.5, 97.25) * mm, "end": v(139.5, 97.25) * mm});
            skLineSegment(sketch, "E120.direction1", {"start": v(-40.5, 94.25) * mm, "end": v(-30.5, 94.25) * mm, "construction": true});
            skLineSegment(sketch, "E121.trimOffspring", {"start": v(-20.5, 94.25) * mm, "end": v(-10.5, 94.25) * mm});
            skLineSegment(sketch, "E122.trimOffspring", {"start": v(-0.5, 94.25) * mm, "end": v(9.5, 94.25) * mm});
            skLineSegment(sketch, "E123.trimOffspring", {"start": v(19.5, 94.25) * mm, "end": v(29.5, 94.25) * mm});
            skLineSegment(sketch, "E124.trimOffspring", {"start": v(39.5, 94.25) * mm, "end": v(49.5, 94.25) * mm});
            skLineSegment(sketch, "E125.trimOffspring", {"start": v(59.5, 94.25) * mm, "end": v(69.5, 94.25) * mm});
            skLineSegment(sketch, "E126.trimOffspring", {"start": v(79.5, 94.25) * mm, "end": v(89.5, 94.25) * mm});
            skLineSegment(sketch, "E127.trimOffspring", {"start": v(99.5, 94.25) * mm, "end": v(109.5, 94.25) * mm});
            skLineSegment(sketch, "E128.trimOffspring", {"start": v(119.5, 94.25) * mm, "end": v(129.5, 94.25) * mm});
            skLineSegment(sketch, "E129", {"start": v(-60.5, 136.25) * mm, "end": v(-60.5, 133.25) * mm});
            skLineSegment(sketch, "E130", {"start": v(-60.5, 133.25) * mm, "end": v(-72.5, 133.25) * mm});
            skLineSegment(sketch, "E131", {"start": v(-50.5, 136.25) * mm, "end": v(-50.5, 133.25) * mm});
            skLineSegment(sketch, "E132", {"start": v(-50.5, 133.25) * mm, "end": v(-40.5, 133.25) * mm});
            skLineSegment(sketch, "E133", {"start": v(-40.5, 133.25) * mm, "end": v(-40.5, 136.25) * mm});
            skLineSegment(sketch, "E134.trimOffspring", {"start": v(-40.5, 136.25) * mm, "end": v(-30.5, 136.25) * mm});
            skLineSegment(sketch, "E135.1.0.0", {"start": v(-30.5, 136.25) * mm, "end": v(-30.5, 133.25) * mm});
            skLineSegment(sketch, "E135.1.0.1", {"start": v(-30.5, 133.25) * mm, "end": v(-20.5, 133.25) * mm});
            skLineSegment(sketch, "E135.1.0.2", {"start": v(-20.5, 133.25) * mm, "end": v(-20.5, 136.25) * mm});
            skLineSegment(sketch, "E135.2.0.0", {"start": v(-10.5, 136.25) * mm, "end": v(-10.5, 133.25) * mm});
            skLineSegment(sketch, "E135.2.0.1", {"start": v(-10.5, 133.25) * mm, "end": v(-0.5, 133.25) * mm});
            skLineSegment(sketch, "E135.2.0.2", {"start": v(-0.5, 133.25) * mm, "end": v(-0.5, 136.25) * mm});
            skLineSegment(sketch, "E135.3.0.0", {"start": v(9.5, 136.25) * mm, "end": v(9.5, 133.25) * mm});
            skLineSegment(sketch, "E135.3.0.1", {"start": v(9.5, 133.25) * mm, "end": v(19.5, 133.25) * mm});
            skLineSegment(sketch, "E135.3.0.2", {"start": v(19.5, 133.25) * mm, "end": v(19.5, 136.25) * mm});
            skLineSegment(sketch, "E135.4.0.0", {"start": v(29.5, 136.25) * mm, "end": v(29.5, 133.25) * mm});
            skLineSegment(sketch, "E135.4.0.1", {"start": v(29.5, 133.25) * mm, "end": v(39.5, 133.25) * mm});
            skLineSegment(sketch, "E135.4.0.2", {"start": v(39.5, 133.25) * mm, "end": v(39.5, 136.25) * mm});
            skLineSegment(sketch, "E135.5.0.0", {"start": v(49.5, 136.25) * mm, "end": v(49.5, 133.25) * mm});
            skLineSegment(sketch, "E135.5.0.1", {"start": v(49.5, 133.25) * mm, "end": v(59.5, 133.25) * mm});
            skLineSegment(sketch, "E135.5.0.2", {"start": v(59.5, 133.25) * mm, "end": v(59.5, 136.25) * mm});
            skLineSegment(sketch, "E135.6.0.0", {"start": v(69.5, 136.25) * mm, "end": v(69.5, 133.25) * mm});
            skLineSegment(sketch, "E135.6.0.1", {"start": v(69.5, 133.25) * mm, "end": v(79.5, 133.25) * mm});
            skLineSegment(sketch, "E135.6.0.2", {"start": v(79.5, 133.25) * mm, "end": v(79.5, 136.25) * mm});
            skLineSegment(sketch, "E135.7.0.0", {"start": v(89.5, 136.25) * mm, "end": v(89.5, 133.25) * mm});
            skLineSegment(sketch, "E135.7.0.1", {"start": v(89.5, 133.25) * mm, "end": v(99.5, 133.25) * mm});
            skLineSegment(sketch, "E135.7.0.2", {"start": v(99.5, 133.25) * mm, "end": v(99.5, 136.25) * mm});
            skLineSegment(sketch, "E135.8.0.0", {"start": v(109.5, 136.25) * mm, "end": v(109.5, 133.25) * mm});
            skLineSegment(sketch, "E135.8.0.1", {"start": v(109.5, 133.25) * mm, "end": v(119.5, 133.25) * mm});
            skLineSegment(sketch, "E135.8.0.2", {"start": v(119.5, 133.25) * mm, "end": v(119.5, 136.25) * mm});
            skLineSegment(sketch, "E135.9.0.0", {"start": v(129.5, 136.25) * mm, "end": v(129.5, 133.25) * mm});
            skLineSegment(sketch, "E135.9.0.1", {"start": v(129.5, 133.25) * mm, "end": v(139.5, 133.25) * mm});
            skLineSegment(sketch, "E135.direction1", {"start": v(-50.5, 133.25) * mm, "end": v(-30.5, 133.25) * mm, "construction": true});
            skLineSegment(sketch, "E136.trimOffspring", {"start": v(-20.5, 136.25) * mm, "end": v(-10.5, 136.25) * mm});
            skLineSegment(sketch, "E137.trimOffspring", {"start": v(-0.5, 136.25) * mm, "end": v(9.5, 136.25) * mm});
            skLineSegment(sketch, "E138.trimOffspring", {"start": v(19.5, 136.25) * mm, "end": v(29.5, 136.25) * mm});
            skLineSegment(sketch, "E139.trimOffspring", {"start": v(39.5, 136.25) * mm, "end": v(49.5, 136.25) * mm});
            skLineSegment(sketch, "E140.trimOffspring", {"start": v(59.5, 136.25) * mm, "end": v(69.5, 136.25) * mm});
            skLineSegment(sketch, "E141.trimOffspring", {"start": v(79.5, 136.25) * mm, "end": v(89.5, 136.25) * mm});
            skLineSegment(sketch, "E142.trimOffspring", {"start": v(99.5, 136.25) * mm, "end": v(109.5, 136.25) * mm});
            skLineSegment(sketch, "E143.trimOffspring", {"start": v(119.5, 136.25) * mm, "end": v(129.5, 136.25) * mm});
            skLineSegment(sketch, "E144", {"start": v(-144.04, 58) * mm, "end": v(-144.04, 55) * mm});
            skLineSegment(sketch, "E145", {"start": v(-144.04, 55) * mm, "end": v(-124.04, 55) * mm});
            skLineSegment(sketch, "E146", {"start": v(-124.04, 55) * mm, "end": v(-124.04, 58) * mm});
            skLineSegment(sketch, "E147.trimOffspring", {"start": v(-144.04, 58) * mm, "end": v(-152.04, 58) * mm});
            skLineSegment(sketch, "E148", {"start": v(-144.04, -82) * mm, "end": v(-144.04, -79) * mm});
            skLineSegment(sketch, "E149", {"start": v(-144.04, -79) * mm, "end": v(-124.04, -79) * mm});
            skLineSegment(sketch, "E150", {"start": v(-124.04, -79) * mm, "end": v(-124.04, -82) * mm});
            skLineSegment(sketch, "E151", {"start": v(-72.5, 133.25) * mm, "end": v(-72.5, 125.25) * mm});
            skLineSegment(sketch, "E152", {"start": v(-72.5, 125.25) * mm, "end": v(-75.5, 125.25) * mm});
            skLineSegment(sketch, "E153", {"start": v(-72.5, 97.25) * mm, "end": v(-72.5, 105.25) * mm});
            skLineSegment(sketch, "E154", {"start": v(-72.5, 105.25) * mm, "end": v(-75.5, 105.25) * mm});
            skPoint(sketch, "E155.orphan", {"position": v(-75.5, 97.25) * mm});
            skLineSegment(sketch, "E156.bottom", {"start": v(-36.5, 118.25) * mm, "end": v(18.5, 118.25) * mm});
            skLineSegment(sketch, "E156.top", {"start": v(-36.5, 100.25) * mm, "end": v(18.5, 100.25) * mm});
            skLineSegment(sketch, "E156.left", {"start": v(-36.5, 118.25) * mm, "end": v(-36.5, 100.25) * mm});
            skLineSegment(sketch, "E156.right", {"start": v(18.5, 118.25) * mm, "end": v(18.5, 100.25) * mm});
            skLineSegment(sketch, "E157.2.0.3", {"start": v(21, -282.98) * mm, "end": v(11, -282.98) * mm});
            skLineSegment(sketch, "E157.3.0.0", {"start": v(6, -282.98) * mm, "end": v(6, -279.98) * mm});
            skLineSegment(sketch, "E157.3.0.1", {"start": v(6, -279.98) * mm, "end": v(-4, -279.98) * mm});
            skLineSegment(sketch, "E157.3.0.2", {"start": v(-4, -279.98) * mm, "end": v(-4, -282.98) * mm});
            skLineSegment(sketch, "E157.3.0.3", {"start": v(-4, -282.98) * mm, "end": v(-14, -282.98) * mm});
            skLineSegment(sketch, "E157.12.0.0", {"start": v(-174, -282.98) * mm, "end": v(-174, -279.98) * mm});
            skLineSegment(sketch, "E157.12.0.1", {"start": v(-174, -279.98) * mm, "end": v(-184, -279.98) * mm});
            skLineSegment(sketch, "E157.12.0.2", {"start": v(-184, -279.98) * mm, "end": v(-184, -282.98) * mm});
            skLineSegment(sketch, "E157.12.0.3", {"start": v(-184, -282.98) * mm, "end": v(-194, -282.98) * mm});
            skLineSegment(sketch, "E158", {"start": v(-199, -282.98) * mm, "end": v(-194, -282.98) * mm});
            skCircle(sketch, "E159", {"center": v(-191, -274.98) * mm, "radius": 1.65 * mm});
            skCircle(sketch, "E160", {"center": v(-67.5, -74) * mm, "radius": 1.65 * mm});
            skCircle(sketch, "E161", {"center": v(-67.5, 50) * mm, "radius": 1.65 * mm});
            skCircle(sketch, "E162", {"center": v(-67.5, 115.25) * mm, "radius": 1.65 * mm});
            skLineSegment(sketch, "E163", {"start": v(-397, -38.15) * mm, "end": v(-397, -35.15) * mm});
            skLineSegment(sketch, "E164", {"start": v(-397, -35.15) * mm, "end": v(-377, -35.15) * mm});
            skLineSegment(sketch, "E165", {"start": v(-377, -35.15) * mm, "end": v(-377, -38.15) * mm});
            skLineSegment(sketch, "E166", {"start": v(-397, 101.85) * mm, "end": v(-397, 98.85) * mm});
            skLineSegment(sketch, "E167", {"start": v(-397, 98.85) * mm, "end": v(-377, 98.85) * mm});
            skLineSegment(sketch, "E168", {"start": v(-377, 98.85) * mm, "end": v(-377, 101.85) * mm});
            skLineSegment(sketch, "E169.trimOffspring", {"start": v(-397, 101.85) * mm, "end": v(-405, 101.85) * mm});
            skCircle(sketch, "E170", {"center": v(57.5, -41) * mm, "radius": 2 * mm});
            skCircle(sketch, "E171", {"center": v(-57.5, -41) * mm, "radius": 2 * mm});
            skCircle(sketch, "E172", {"center": v(57.5, 41) * mm, "radius": 2 * mm});
            skCircle(sketch, "E173", {"center": v(-57.5, 41) * mm, "radius": 2 * mm});
            skCircle(sketch, "E174", {"center": v(-89, -274.98) * mm, "radius": 1.65 * mm});
            skCircle(sketch, "E175", {"center": v(-191, -150.98) * mm, "radius": 1.65 * mm});
            skCircle(sketch, "E176", {"center": v(-89, -150.98) * mm, "radius": 1.65 * mm});
            skCircle(sketch, "E177", {"center": v(13, -150.98) * mm, "radius": 1.65 * mm});
            skCircle(sketch, "E178", {"center": v(34.5, -74) * mm, "radius": 1.65 * mm});
            skCircle(sketch, "E179", {"center": v(136.5, -74) * mm, "radius": 1.65 * mm});
            skCircle(sketch, "E180", {"center": v(136.5, 50) * mm, "radius": 1.65 * mm});
            skCircle(sketch, "E181", {"center": v(34.5, 50) * mm, "radius": 1.65 * mm});
            skCircle(sketch, "E182", {"center": v(-40, -60) * mm, "radius": 5 * mm});
            skCircle(sketch, "E183.1.0.0", {"center": v(0, -60) * mm, "radius": 5 * mm});
            skCircle(sketch, "E183.2.0.0", {"center": v(40, -60) * mm, "radius": 5 * mm});
            skLineSegment(sketch, "E183.direction1", {"start": v(-40, -60) * mm, "end": v(0, -60) * mm, "construction": true});
            skLineSegment(sketch, "E184", {"start": v(144.5, 55) * mm, "end": v(144.5, 43) * mm});
            skLineSegment(sketch, "E185", {"start": v(139.5, 133.25) * mm, "end": v(141.5, 133.25) * mm});
            skLineSegment(sketch, "E186", {"start": v(141.5, 133.25) * mm, "end": v(141.5, 125.25) * mm});
            skLineSegment(sketch, "E187", {"start": v(141.5, 125.25) * mm, "end": v(144.5, 125.25) * mm});
            skLineSegment(sketch, "E188", {"start": v(144.5, 125.25) * mm, "end": v(144.5, 105.25) * mm});
            skLineSegment(sketch, "E189", {"start": v(144.5, 105.25) * mm, "end": v(141.5, 105.25) * mm});
            skLineSegment(sketch, "E190", {"start": v(141.5, 105.25) * mm, "end": v(141.5, 97.25) * mm});
            skLineSegment(sketch, "E191", {"start": v(141.5, 97.25) * mm, "end": v(139.5, 97.25) * mm});
            skLineSegment(sketch, "E192", {"start": v(144.5, -67) * mm, "end": v(141.5, -67) * mm});
            skLineSegment(sketch, "E193", {"start": v(141.5, -67) * mm, "end": v(141.5, -57) * mm});
            skLineSegment(sketch, "E194", {"start": v(141.5, -57) * mm, "end": v(144.5, -57) * mm});
            skLineSegment(sketch, "E195", {"start": v(144.5, -47) * mm, "end": v(141.5, -47) * mm});
            skLineSegment(sketch, "E196", {"start": v(141.5, -47) * mm, "end": v(141.5, -37) * mm});
            skLineSegment(sketch, "E197", {"start": v(141.5, -37) * mm, "end": v(144.5, -37) * mm});
            skLineSegment(sketch, "E198", {"start": v(144.5, -27) * mm, "end": v(141.5, -27) * mm});
            skLineSegment(sketch, "E199", {"start": v(141.5, -27) * mm, "end": v(141.5, -17) * mm});
            skLineSegment(sketch, "E200", {"start": v(141.5, -17) * mm, "end": v(144.5, -17) * mm});
            skLineSegment(sketch, "E201", {"start": v(144.5, -7) * mm, "end": v(141.5, -7) * mm});
            skLineSegment(sketch, "E202", {"start": v(141.5, -7) * mm, "end": v(141.5, 3) * mm});
            skLineSegment(sketch, "E203", {"start": v(141.5, 3) * mm, "end": v(144.5, 3) * mm});
            skLineSegment(sketch, "E204", {"start": v(144.5, 13) * mm, "end": v(141.5, 13) * mm});
            skLineSegment(sketch, "E205", {"start": v(141.5, 13) * mm, "end": v(141.5, 23) * mm});
            skLineSegment(sketch, "E206", {"start": v(141.5, 23) * mm, "end": v(144.5, 23) * mm});
            skLineSegment(sketch, "E207", {"start": v(144.5, 33) * mm, "end": v(141.5, 33) * mm});
            skLineSegment(sketch, "E208", {"start": v(141.5, 33) * mm, "end": v(141.5, 43) * mm});
            skLineSegment(sketch, "E209", {"start": v(141.5, 43) * mm, "end": v(144.5, 43) * mm});
            skLineSegment(sketch, "E210.trimOffspring", {"start": v(144.5, 33) * mm, "end": v(144.5, 23) * mm});
            skLineSegment(sketch, "E211.trimOffspring", {"start": v(144.5, 13) * mm, "end": v(144.5, 3) * mm});
            skLineSegment(sketch, "E212.trimOffspring", {"start": v(144.5, -7) * mm, "end": v(144.5, -17) * mm});
            skLineSegment(sketch, "E213.trimOffspring", {"start": v(144.5, -27) * mm, "end": v(144.5, -37) * mm});
            skLineSegment(sketch, "E214.trimOffspring", {"start": v(144.5, -47) * mm, "end": v(144.5, -57) * mm});
            skLineSegment(sketch, "E215.trimOffspring", {"start": v(144.5, -67) * mm, "end": v(144.5, -79) * mm});
            skLineSegment(sketch, "E216", {"start": v(6, -282.98) * mm, "end": v(11, -282.98) * mm});
            skLineSegment(sketch, "E217", {"start": v(21, -157.98) * mm, "end": v(18, -157.98) * mm});
            skLineSegment(sketch, "E218", {"start": v(18, -157.98) * mm, "end": v(18, -167.98) * mm});
            skLineSegment(sketch, "E219", {"start": v(18, -167.98) * mm, "end": v(21, -167.98) * mm});
            skLineSegment(sketch, "E220", {"start": v(21, -177.98) * mm, "end": v(18, -177.98) * mm});
            skLineSegment(sketch, "E221", {"start": v(18, -177.98) * mm, "end": v(18, -187.98) * mm});
            skLineSegment(sketch, "E222", {"start": v(18, -187.98) * mm, "end": v(21, -187.98) * mm});
            skLineSegment(sketch, "E223", {"start": v(21, -197.98) * mm, "end": v(18, -197.98) * mm});
            skLineSegment(sketch, "E224", {"start": v(18, -197.98) * mm, "end": v(18, -207.98) * mm});
            skLineSegment(sketch, "E225", {"start": v(18, -207.98) * mm, "end": v(21, -207.98) * mm});
            skLineSegment(sketch, "E226", {"start": v(21, -217.98) * mm, "end": v(18, -217.98) * mm});
            skLineSegment(sketch, "E227", {"start": v(18, -217.98) * mm, "end": v(18, -227.98) * mm});
            skLineSegment(sketch, "E228", {"start": v(18, -227.98) * mm, "end": v(21, -227.98) * mm});
            skLineSegment(sketch, "E229.trimOffspring", {"start": v(21, -207.98) * mm, "end": v(21, -217.98) * mm});
            skLineSegment(sketch, "E230.trimOffspring", {"start": v(21, -187.98) * mm, "end": v(21, -197.98) * mm});
            skLineSegment(sketch, "E231.trimOffspring", {"start": v(21, -167.98) * mm, "end": v(21, -177.98) * mm});
            skLineSegment(sketch, "E232", {"start": v(21, -282.98) * mm, "end": v(21, -267.98) * mm});
            skLineSegment(sketch, "E233", {"start": v(21, -267.98) * mm, "end": v(18, -267.98) * mm});
            skLineSegment(sketch, "E234", {"start": v(18, -267.98) * mm, "end": v(18, -257.98) * mm});
            skLineSegment(sketch, "E235", {"start": v(18, -257.98) * mm, "end": v(21, -257.98) * mm});
            skLineSegment(sketch, "E236", {"start": v(21, -257.98) * mm, "end": v(21, -247.98) * mm});
            skLineSegment(sketch, "E237", {"start": v(21, -247.98) * mm, "end": v(18, -247.98) * mm});
            skLineSegment(sketch, "E238", {"start": v(18, -247.98) * mm, "end": v(18, -237.98) * mm});
            skLineSegment(sketch, "E239", {"start": v(18, -237.98) * mm, "end": v(21, -237.98) * mm});
            skLineSegment(sketch, "E240", {"start": v(21, -237.98) * mm, "end": v(21, -227.98) * mm});
            skLineSegment(sketch, "E241", {"start": v(21, -157.98) * mm, "end": v(21, -142.98) * mm});
            skLineSegment(sketch, "E242", {"start": v(-174, -282.98) * mm, "end": v(-164, -282.98) * mm});
            skLineSegment(sketch, "E243", {"start": v(-164, -282.98) * mm, "end": v(-164, -279.98) * mm});
            skLineSegment(sketch, "E244", {"start": v(-164, -279.98) * mm, "end": v(-154, -279.98) * mm});
            skLineSegment(sketch, "E245", {"start": v(-154, -279.98) * mm, "end": v(-154, -282.98) * mm});
            skLineSegment(sketch, "E246", {"start": v(-154, -282.98) * mm, "end": v(-144, -282.98) * mm});
            skLineSegment(sketch, "E247", {"start": v(-144, -282.98) * mm, "end": v(-144, -279.98) * mm});
            skLineSegment(sketch, "E248", {"start": v(-144, -279.98) * mm, "end": v(-134, -279.98) * mm});
            skLineSegment(sketch, "E249", {"start": v(-134, -279.98) * mm, "end": v(-134, -282.98) * mm});
            skLineSegment(sketch, "E250", {"start": v(-134, -282.98) * mm, "end": v(-124, -282.98) * mm});
            skLineSegment(sketch, "E251", {"start": v(-124, -282.98) * mm, "end": v(-124, -279.98) * mm});
            skLineSegment(sketch, "E252", {"start": v(-124, -279.98) * mm, "end": v(-114, -279.98) * mm});
            skLineSegment(sketch, "E253", {"start": v(-114, -279.98) * mm, "end": v(-114, -282.98) * mm});
            skLineSegment(sketch, "E254", {"start": v(-114, -282.98) * mm, "end": v(-104, -282.98) * mm});
            skLineSegment(sketch, "E255", {"start": v(-104, -282.98) * mm, "end": v(-104, -279.98) * mm});
            skLineSegment(sketch, "E256", {"start": v(-104, -279.98) * mm, "end": v(-94, -279.98) * mm});
            skLineSegment(sketch, "E257", {"start": v(-94, -279.98) * mm, "end": v(-94, -282.98) * mm});
            skLineSegment(sketch, "E258", {"start": v(-94, -282.98) * mm, "end": v(-84, -282.98) * mm});
            skLineSegment(sketch, "E259", {"start": v(-84, -282.98) * mm, "end": v(-84, -279.98) * mm});
            skLineSegment(sketch, "E260", {"start": v(-84, -279.98) * mm, "end": v(-74, -279.98) * mm});
            skLineSegment(sketch, "E261", {"start": v(-74, -279.98) * mm, "end": v(-74, -282.98) * mm});
            skLineSegment(sketch, "E262", {"start": v(-74, -282.98) * mm, "end": v(-64, -282.98) * mm});
            skLineSegment(sketch, "E263", {"start": v(-64, -282.98) * mm, "end": v(-64, -279.98) * mm});
            skLineSegment(sketch, "E264", {"start": v(-64, -279.98) * mm, "end": v(-54, -279.98) * mm});
            skLineSegment(sketch, "E265", {"start": v(-54, -279.98) * mm, "end": v(-54, -282.98) * mm});
            skLineSegment(sketch, "E266", {"start": v(-54, -282.98) * mm, "end": v(-44, -282.98) * mm});
            skLineSegment(sketch, "E267", {"start": v(-44, -282.98) * mm, "end": v(-44, -279.98) * mm});
            skLineSegment(sketch, "E268", {"start": v(-44, -279.98) * mm, "end": v(-34, -279.98) * mm});
            skLineSegment(sketch, "E269", {"start": v(-34, -279.98) * mm, "end": v(-34, -282.98) * mm});
            skLineSegment(sketch, "E270", {"start": v(-34, -282.98) * mm, "end": v(-24, -282.98) * mm});
            skLineSegment(sketch, "E271", {"start": v(-24, -282.98) * mm, "end": v(-24, -279.98) * mm});
            skLineSegment(sketch, "E272", {"start": v(-24, -279.98) * mm, "end": v(-14, -279.98) * mm});
            skLineSegment(sketch, "E273", {"start": v(-14, -279.98) * mm, "end": v(-14, -282.98) * mm});
            skCircle(sketch, "E274", {"center": v(13, -274.98) * mm, "radius": 1.65 * mm});
            skCircle(sketch, "E275", {"center": v(136.5, 115.25) * mm, "radius": 1.65 * mm});
            skCircle(sketch, "E276", {"center": v(104.5, -44) * mm, "radius": 10.15 * mm});
            skLineSegment(sketch, "E277", {"start": v(109.5, -82) * mm, "end": v(119.5, -82) * mm});
            skLineSegment(sketch, "E278", {"start": v(119.5, -82) * mm, "end": v(119.5, -79) * mm});
            skLineSegment(sketch, "E279", {"start": v(119.5, -79) * mm, "end": v(129.5, -79) * mm});
            skLineSegment(sketch, "E280", {"start": v(129.5, -79) * mm, "end": v(129.5, -82) * mm});
            skCircle(sketch, "E281", {"center": v(84.5, -2) * mm, "radius": 5.5 * mm});
            skCircle(sketch, "E282.0.1.0", {"center": v(84.5, 18) * mm, "radius": 5.5 * mm});
            skCircle(sketch, "E282.1.0.0", {"center": v(104.5, -2) * mm, "radius": 5.5 * mm});
            skCircle(sketch, "E282.1.1.0", {"center": v(104.5, 18) * mm, "radius": 5.5 * mm});
            skCircle(sketch, "E282.2.0.0", {"center": v(124.5, -2) * mm, "radius": 5.5 * mm});
            skCircle(sketch, "E282.2.1.0", {"center": v(124.5, 18) * mm, "radius": 5.5 * mm});
            skLineSegment(sketch, "E282.direction1", {"start": v(84.5, -2) * mm, "end": v(104.5, -2) * mm, "construction": true});
            skLineSegment(sketch, "E282.direction2", {"start": v(84.5, -2) * mm, "end": v(84.5, 18) * mm, "construction": true});
            skCircle(sketch, "E283", {"center": v(104.5, -59) * mm, "radius": 2 * mm});
            skCircle(sketch, "E284", {"center": v(91.5, -36.5) * mm, "radius": 2 * mm});
            skCircle(sketch, "E285", {"center": v(117.5, -36.5) * mm, "radius": 2 * mm});
            skLineSegment(sketch, "E286", {"start": v(-4.5, -38) * mm, "end": v(-4.5, -40) * mm});
            skLineSegment(sketch, "E287", {"start": v(-4.5, -40) * mm, "end": v(15.5, -40) * mm});
            skLineSegment(sketch, "E288", {"start": v(15.5, -40) * mm, "end": v(15.5, -38) * mm});
            skLineSegment(sketch, "E289.trimOffspring", {"start": v(15.5, -38) * mm, "end": v(60.5, -38) * mm});
            skLineSegment(sketch, "E290", {"start": v(-155.04, -82) * mm, "end": v(-123.54, -100.19) * mm});
            skLineSegment(sketch, "E291", {"start": v(-116.04, -82) * mm, "end": v(-116.04, -95.86) * mm});
            skArc(sketch, "E292.filletArc", {"start": v(-123.54, -100.19) * mm, "mid": v(-118.54, -100.19) * mm, "end": v(-116.04, -95.86) * mm});
            skLineSegment(sketch, "E293", {"start": v(-155.03, -82) * mm, "end": v(-152.04, -82) * mm});
            skLineSegment(sketch, "E294", {"start": v(-144.04, -82) * mm, "end": v(-124.04, -82) * mm});
            skLineSegment(sketch, "E295", {"start": v(-408.04, -38.15) * mm, "end": v(-376.5, -56.36) * mm});
            skLineSegment(sketch, "E296", {"start": v(-369, -38.15) * mm, "end": v(-369, -52.03) * mm});
            skArc(sketch, "E297.filletArc", {"start": v(-376.5, -56.36) * mm, "mid": v(-371.5, -56.36) * mm, "end": v(-369, -52.03) * mm});
            skLineSegment(sketch, "E298", {"start": v(-397, -38.15) * mm, "end": v(-377, -38.15) * mm});
            skLineSegment(sketch, "E299", {"start": v(-408.03, -38.15) * mm, "end": v(-405, -38.15) * mm});
            skPoint(sketch, "E300.visualSharp", {"position": v(-408.04, -38.15) * mm});
            skArc(sketch, "E300.filletArc", {"start": v(-408.04, -38.14) * mm, "mid": v(-408.04, -38.15) * mm, "end": v(-408.03, -38.15) * mm});
            skPoint(sketch, "E301.visualSharp", {"position": v(-155.04, -82) * mm});
            skArc(sketch, "E301.filletArc", {"start": v(-155.04, -82) * mm, "mid": v(-155.03, -82) * mm, "end": v(-155.03, -82) * mm});
            skCircle(sketch, "E302", {"center": v(-97.2, -206.4) * mm, "radius": 34.64 * mm});
            skSolve(sketch);
        }
        {
            var Q0;
            Q0=makeQuery(id+"FEK8cSwkQIZ1cOT_0.opExtrude","CAP_FACE",FACE,{"disambiguationData":[OSD([sQuery(id+"F0.wireOp",EDGE,"93LQwlPU-J4Sr-fsPR-k0XL-sL3KZKnedlBF.bottom"),sQuery(id+"F0.wireOp",EDGE,"93LQwlPU-J4Sr-fsPR-k0XL-sL3KZKnedlBF.top"),sQuery(id+"F0.wireOp",EDGE,"93LQwlPU-J4Sr-fsPR-k0XL-sL3KZKnedlBF.left"),sQuery(id+"F0.wireOp",EDGE,"93LQwlPU-J4Sr-fsPR-k0XL-sL3KZKnedlBF.right")])],"isStart":false});
            var sketch = newSketch(context, id + "F1", { "sketchPlane" : qUnion([Q0])});
            skCircle(sketch, "E303", {"center": v(-100.17, 114.25) * mm, "radius": 1.65 * mm});
            skSolve(sketch);
        }
        {
            var Q0;
            Q0=makeQuery(id+"F0.imprint","IMPRINT",FACE,{"disambiguationData":[TD([[makeQuery(id+"F0.imprint","IMPRINT",EDGE,{"derivedFrom":sQuery(id+"F0.wireOp",EDGE,"E0.bottom")}),1.0]])]});
            extrude(context, id + "F2", {"entities" : qUnion([Q0]), "depth" : 3 * mm, "offsetDistance" : 25 * mm});
        }
        {
            var Q0;
            Q0 = qSketchRegion(id + "F1", true);
            var Q1;
            Q1 = qSketchRegion(id + "F0", true);
            extrude(context, id + "F3", {"entities" : qUnion([Q0, Q1]), "operationType" : NewBodyOperationType.ADD, "depth" : 3 * mm, "offsetDistance" : 25 * mm});
        }
    });
